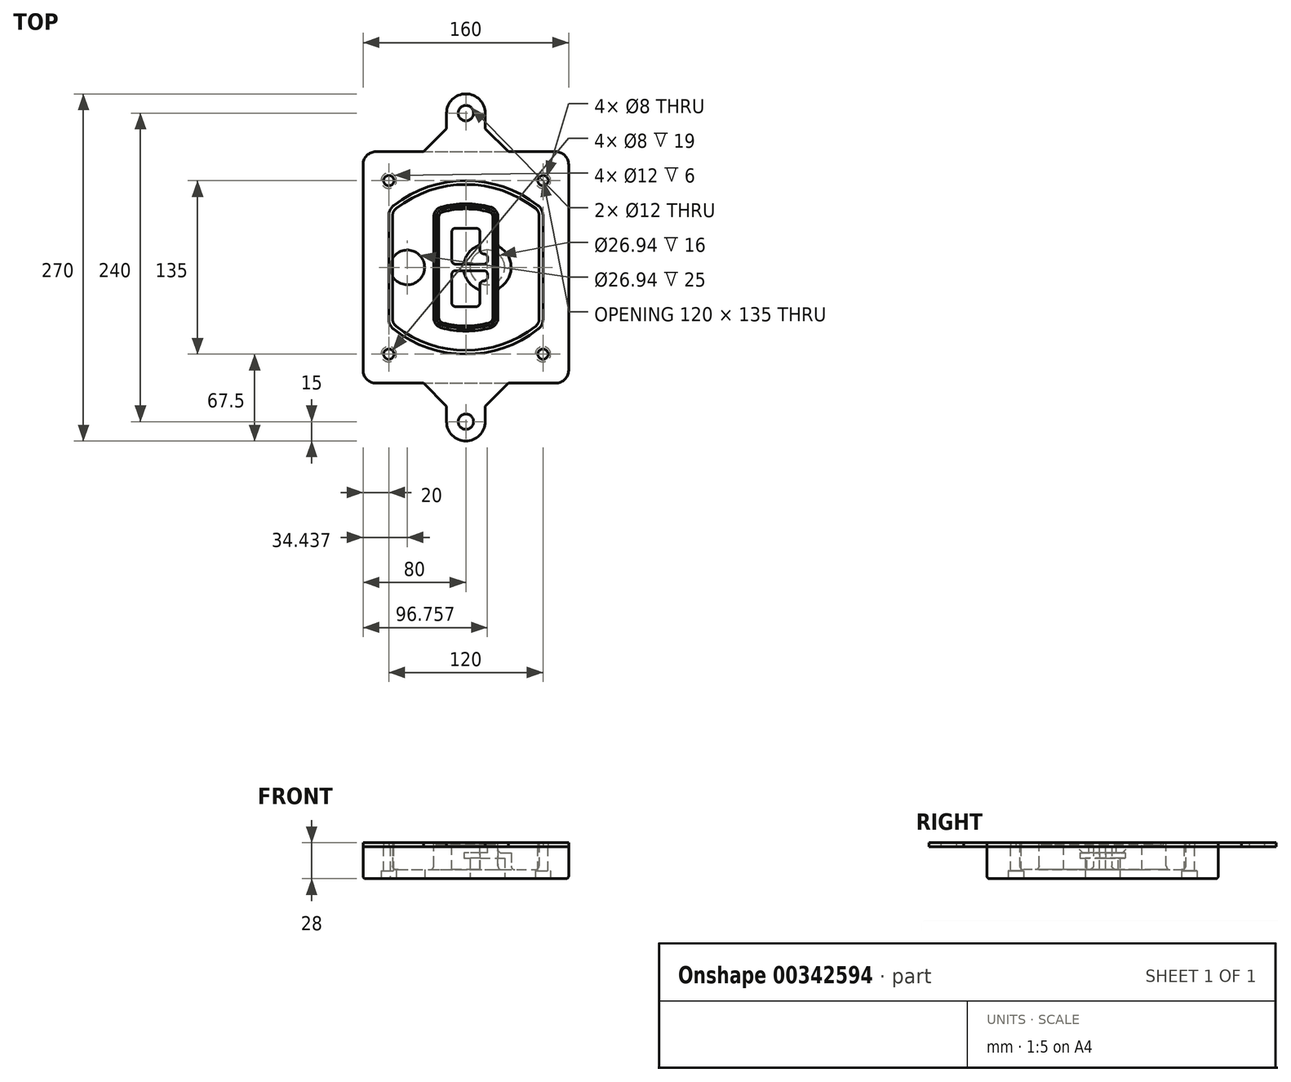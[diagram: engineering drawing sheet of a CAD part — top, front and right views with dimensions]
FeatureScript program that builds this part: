
annotation { "Feature Type Name" : "Feature", "Feature Type Description" : "" }
export const myFeature = defineFeature(function(context is Context, id is Id, definition is map)
    precondition{}
    {
        {
            var Q0;
            Q0=qCreatedBy(makeId("Top.planeOp"),FACE);
            var sketch = newSketch(context, id + "F0", { "sketchPlane" : qUnion([Q0])});
            skPoint(sketch, "E0.rect.middle", {"position": v(0, 0) * mm});
            skLineSegment(sketch, "E1.bottom", {"start": v(-70, -90) * mm, "end": v(70, -90) * mm});
            skLineSegment(sketch, "E1.top", {"start": v(-70, 90) * mm, "end": v(70, 90) * mm});
            skLineSegment(sketch, "E1.left", {"start": v(-80, -80) * mm, "end": v(-80, 80) * mm});
            skLineSegment(sketch, "E1.right", {"start": v(80, -80) * mm, "end": v(80, 80) * mm});
            skLineSegment(sketch, "E2", {"start": v(-80, 90) * mm, "end": v(80, -90) * mm, "construction": true});
            skLineSegment(sketch, "E3", {"start": v(80, 90) * mm, "end": v(-80, -90) * mm, "construction": true});
            skCircle(sketch, "E4", {"center": v(-60, 67.5) * mm, "radius": 4 * mm});
            skCircle(sketch, "E5", {"center": v(60, 67.5) * mm, "radius": 4 * mm});
            skCircle(sketch, "E6", {"center": v(60, -67.5) * mm, "radius": 4 * mm});
            skCircle(sketch, "E7", {"center": v(-60, -67.5) * mm, "radius": 4 * mm});
            skLineSegment(sketch, "E8", {"start": v(-60, 67.5) * mm, "end": v(60, 67.5) * mm, "construction": true});
            skLineSegment(sketch, "E9", {"start": v(60, 67.5) * mm, "end": v(60, -67.5) * mm, "construction": true});
            skLineSegment(sketch, "E10", {"start": v(60, -67.5) * mm, "end": v(-60, -67.5) * mm, "construction": true});
            skLineSegment(sketch, "E11", {"start": v(-60, -67.5) * mm, "end": v(-60, 67.5) * mm, "construction": true});
            skLineSegment(sketch, "E12", {"start": v(-60, 40.3) * mm, "end": v(-60, -40.3) * mm});
            skLineSegment(sketch, "E13", {"start": v(60, 40.3) * mm, "end": v(60, -40.3) * mm});
            skArc(sketch, "E14", {"start": v(56.15, 48.18) * mm, "mid": v(0, 67.5) * mm, "end": v(-56.15, 48.18) * mm});
            skArc(sketch, "E15", {"start": v(-56.15, -48.18) * mm, "mid": v(0, -67.5) * mm, "end": v(56.15, -48.18) * mm});
            skLineSegment(sketch, "E16", {"start": v(-60, 0) * mm, "end": v(60, 0) * mm, "construction": true});
            skPoint(sketch, "E17.visualSharp", {"position": v(-60, -45) * mm});
            skArc(sketch, "E17.filletArc", {"start": v(-60, -40.3) * mm, "mid": v(-58.99, -44.68) * mm, "end": v(-56.15, -48.18) * mm});
            skPoint(sketch, "E18.visualSharp", {"position": v(-60, 45) * mm});
            skArc(sketch, "E18.filletArc", {"start": v(-56.15, 48.18) * mm, "mid": v(-58.99, 44.68) * mm, "end": v(-60, 40.3) * mm});
            skPoint(sketch, "E19.visualSharp", {"position": v(60, 45) * mm});
            skArc(sketch, "E19.filletArc", {"start": v(60, 40.3) * mm, "mid": v(58.99, 44.68) * mm, "end": v(56.15, 48.18) * mm});
            skPoint(sketch, "E20.visualSharp", {"position": v(60, -45) * mm});
            skArc(sketch, "E20.filletArc", {"start": v(56.15, -48.18) * mm, "mid": v(58.99, -44.68) * mm, "end": v(60, -40.3) * mm});
            skPoint(sketch, "E21.visualSharp", {"position": v(-80, 90) * mm});
            skArc(sketch, "E21.filletArc", {"start": v(-70, 90) * mm, "mid": v(-77.07, 87.07) * mm, "end": v(-80, 80) * mm});
            skPoint(sketch, "E22.visualSharp", {"position": v(80, 90) * mm});
            skArc(sketch, "E22.filletArc", {"start": v(80, 80) * mm, "mid": v(77.07, 87.07) * mm, "end": v(70, 90) * mm});
            skPoint(sketch, "E23.visualSharp", {"position": v(80, -90) * mm});
            skArc(sketch, "E23.filletArc", {"start": v(70, -90) * mm, "mid": v(77.07, -87.07) * mm, "end": v(80, -80) * mm});
            skPoint(sketch, "E24.visualSharp", {"position": v(-80, -90) * mm});
            skArc(sketch, "E24.filletArc", {"start": v(-80, -80) * mm, "mid": v(-77.07, -87.07) * mm, "end": v(-70, -90) * mm});
            skArc(sketch, "E25.0", {"start": v(57, 40.3) * mm, "mid": v(56.3, 43.36) * mm, "end": v(54.3, 45.81) * mm});
            skLineSegment(sketch, "E25.1", {"start": v(57, 40.3) * mm, "end": v(57, -40.3) * mm});
            skArc(sketch, "E25.2", {"start": v(54.3, -45.81) * mm, "mid": v(56.3, -43.36) * mm, "end": v(57, -40.3) * mm});
            skArc(sketch, "E25.3", {"start": v(-54.3, -45.81) * mm, "mid": v(0, -64.5) * mm, "end": v(54.3, -45.81) * mm});
            skArc(sketch, "E25.4", {"start": v(-57, -40.3) * mm, "mid": v(-56.3, -43.36) * mm, "end": v(-54.3, -45.81) * mm});
            skArc(sketch, "E25.5", {"start": v(54.3, 45.81) * mm, "mid": v(0, 64.5) * mm, "end": v(-54.3, 45.81) * mm});
            skLineSegment(sketch, "E25.6", {"start": v(-57, 40.3) * mm, "end": v(-57, -40.3) * mm});
            skArc(sketch, "E25.7", {"start": v(-54.3, 45.81) * mm, "mid": v(-56.3, 43.36) * mm, "end": v(-57, 40.3) * mm});
            skArc(sketch, "E26.0", {"start": v(-58.62, 51.33) * mm, "mid": v(-62.58, 46.43) * mm, "end": v(-64, 40.3) * mm});
            skArc(sketch, "E26.1", {"start": v(58.62, 51.33) * mm, "mid": v(0, 71.5) * mm, "end": v(-58.62, 51.33) * mm});
            skArc(sketch, "E26.2", {"start": v(64, 40.3) * mm, "mid": v(62.58, 46.43) * mm, "end": v(58.62, 51.33) * mm});
            skLineSegment(sketch, "E26.3", {"start": v(64, 40.3) * mm, "end": v(64, -40.3) * mm});
            skArc(sketch, "E26.4", {"start": v(58.62, -51.33) * mm, "mid": v(62.58, -46.43) * mm, "end": v(64, -40.3) * mm});
            skLineSegment(sketch, "E26.5", {"start": v(-64, 40.3) * mm, "end": v(-64, -40.3) * mm});
            skArc(sketch, "E26.6", {"start": v(-58.62, -51.33) * mm, "mid": v(0, -71.5) * mm, "end": v(58.62, -51.33) * mm});
            skArc(sketch, "E26.7", {"start": v(-64, -40.3) * mm, "mid": v(-62.58, -46.43) * mm, "end": v(-58.62, -51.33) * mm});
            skSolve(sketch);
        }
        {
            var Q0;
            Q0=makeQuery(id+"F0.imprint","IMPRINT",FACE,{"disambiguationData":[TD([[makeQuery(id+"F0.imprint","IMPRINT",EDGE,{"derivedFrom":sQuery(id+"F0.wireOp",EDGE,"E1.bottom")}),1.0]])]});
            var Q1;
            Q1=makeQuery(id+"F0.imprint","IMPRINT",FACE,{"disambiguationData":[TD([[makeQuery(id+"F0.imprint","IMPRINT",EDGE,{"derivedFrom":sQuery(id+"F0.wireOp",EDGE,"E12")}),1.0]])]});
            var Q2;
            Q2=makeQuery(id+"F0.imprint","IMPRINT",FACE,{"disambiguationData":[TD([[makeQuery(id+"F0.imprint","IMPRINT",EDGE,{"derivedFrom":sQuery(id+"F0.wireOp",EDGE,"E25.0")}),1.0]])]});
            var Q3;
            Q3=makeQuery(id+"F0.imprint","IMPRINT",FACE,{"disambiguationData":[TD([[makeQuery(id+"F0.imprint","IMPRINT",EDGE,{"derivedFrom":sQuery(id+"F0.wireOp",EDGE,"E12")}),-1.0]])]});
            extrude(context, id + "F1", {"entities" : qUnion([Q0, Q1, Q2, Q3]), "oppositeDirection" : true, "depth" : 25 * mm});
        }
        {
            var Q0;
            Q0=makeQuery(id+"F0.imprint","IMPRINT",FACE,{"disambiguationData":[TD([[makeQuery(id+"F0.imprint","IMPRINT",EDGE,{"derivedFrom":sQuery(id+"F0.wireOp",EDGE,"E12")}),1.0]])]});
            extrude(context, id + "F2", {"entities" : qUnion([Q0]), "operationType" : NewBodyOperationType.ADD, "depth" : 3 * mm});
        }
        {
            var Q0;
            Q0=makeQuery(id+"F0.imprint","IMPRINT",FACE,{"disambiguationData":[TD([[makeQuery(id+"F0.imprint","IMPRINT",EDGE,{"derivedFrom":sQuery(id+"F0.wireOp",EDGE,"E25.0")}),1.0]])]});
            extrude(context, id + "F3", {"entities" : qUnion([Q0]), "operationType" : NewBodyOperationType.REMOVE, "oppositeDirection" : true, "depth" : 18 * mm});
        }
        {
            var Q0;
            Q0=makeQuery(id+"F2.opExtrude","CAP_FACE",FACE,{"disambiguationData":[OSD([sQuery(id+"F0.wireOp",EDGE,"E12"),sQuery(id+"F0.wireOp",EDGE,"E13"),sQuery(id+"F0.wireOp",EDGE,"E14"),sQuery(id+"F0.wireOp",EDGE,"E15"),sQuery(id+"F0.wireOp",EDGE,"E17.filletArc"),sQuery(id+"F0.wireOp",EDGE,"E18.filletArc"),sQuery(id+"F0.wireOp",EDGE,"E19.filletArc"),sQuery(id+"F0.wireOp",EDGE,"E20.filletArc"),sQuery(id+"F0.wireOp",EDGE,"E25.0"),sQuery(id+"F0.wireOp",EDGE,"E25.1"),sQuery(id+"F0.wireOp",EDGE,"E25.2"),sQuery(id+"F0.wireOp",EDGE,"E25.3"),sQuery(id+"F0.wireOp",EDGE,"E25.4"),sQuery(id+"F0.wireOp",EDGE,"E25.5"),sQuery(id+"F0.wireOp",EDGE,"E25.6"),sQuery(id+"F0.wireOp",EDGE,"E25.7")])],"isStart":false});
            var sketch = newSketch(context, id + "F4", { "sketchPlane" : qUnion([Q0])});
            skArc(sketch, "E27.0", {"start": v(-19.08, -46.97) * mm, "mid": v(0, -49.5) * mm, "end": v(19.08, -46.97) * mm});
            skArc(sketch, "E28.0", {"start": v(19.08, 46.97) * mm, "mid": v(0, 49.5) * mm, "end": v(-19.08, 46.97) * mm});
            skLineSegment(sketch, "E29", {"start": v(-25, 39.25) * mm, "end": v(-25, -39.25) * mm});
            skLineSegment(sketch, "E30", {"start": v(25, 39.25) * mm, "end": v(25, -39.25) * mm});
            skLineSegment(sketch, "E31", {"start": v(-25, 45.1) * mm, "end": v(25, 45.1) * mm, "construction": true});
            skLineSegment(sketch, "E32", {"start": v(-25, -45.1) * mm, "end": v(25, -45.1) * mm, "construction": true});
            skPoint(sketch, "E33.visualSharp", {"position": v(-25, 45.1) * mm});
            skArc(sketch, "E33.filletArc", {"start": v(-19.08, 46.97) * mm, "mid": v(-23.35, 44.11) * mm, "end": v(-25, 39.25) * mm});
            skPoint(sketch, "E34.visualSharp", {"position": v(25, 45.1) * mm});
            skArc(sketch, "E34.filletArc", {"start": v(25, 39.25) * mm, "mid": v(23.35, 44.11) * mm, "end": v(19.08, 46.97) * mm});
            skPoint(sketch, "E35.visualSharp", {"position": v(25, -45.1) * mm});
            skArc(sketch, "E35.filletArc", {"start": v(19.08, -46.97) * mm, "mid": v(23.35, -44.11) * mm, "end": v(25, -39.25) * mm});
            skPoint(sketch, "E36.visualSharp", {"position": v(-25, -45.1) * mm});
            skArc(sketch, "E36.filletArc", {"start": v(-25, -39.25) * mm, "mid": v(-23.35, -44.11) * mm, "end": v(-19.08, -46.97) * mm});
            skArc(sketch, "E37.0", {"start": v(54.3, 45.81) * mm, "mid": v(0, 64.5) * mm, "end": v(-54.3, 45.81) * mm});
            skArc(sketch, "E37.1", {"start": v(-54.3, 45.81) * mm, "mid": v(-56.3, 43.36) * mm, "end": v(-57, 40.3) * mm});
            skLineSegment(sketch, "E37.2", {"start": v(-57, 40.3) * mm, "end": v(-57, -40.3) * mm});
            skArc(sketch, "E37.3", {"start": v(-57, -40.3) * mm, "mid": v(-56.3, -43.36) * mm, "end": v(-54.3, -45.81) * mm});
            skArc(sketch, "E37.4", {"start": v(-54.3, -45.81) * mm, "mid": v(0, -64.5) * mm, "end": v(54.3, -45.81) * mm});
            skArc(sketch, "E37.5", {"start": v(54.3, -45.81) * mm, "mid": v(56.3, -43.36) * mm, "end": v(57, -40.3) * mm});
            skLineSegment(sketch, "E37.6", {"start": v(57, 40.3) * mm, "end": v(57, -40.3) * mm});
            skArc(sketch, "E37.7", {"start": v(57, 40.3) * mm, "mid": v(56.3, 43.36) * mm, "end": v(54.3, 45.81) * mm});
            skLineSegment(sketch, "E38.0", {"start": v(23, 39.25) * mm, "end": v(23, -39.25) * mm});
            skArc(sketch, "E38.1", {"start": v(18.56, -45.04) * mm, "mid": v(21.76, -42.9) * mm, "end": v(23, -39.25) * mm});
            skArc(sketch, "E38.2", {"start": v(-18.56, -45.04) * mm, "mid": v(0, -47.5) * mm, "end": v(18.56, -45.04) * mm});
            skArc(sketch, "E38.3", {"start": v(-23, -39.25) * mm, "mid": v(-21.76, -42.9) * mm, "end": v(-18.56, -45.04) * mm});
            skLineSegment(sketch, "E38.4", {"start": v(-23, 39.25) * mm, "end": v(-23, -39.25) * mm});
            skArc(sketch, "E38.5", {"start": v(23, 39.25) * mm, "mid": v(21.76, 42.9) * mm, "end": v(18.56, 45.04) * mm});
            skArc(sketch, "E38.6", {"start": v(-18.56, 45.04) * mm, "mid": v(-21.76, 42.9) * mm, "end": v(-23, 39.25) * mm});
            skArc(sketch, "E38.7", {"start": v(18.56, 45.04) * mm, "mid": v(0, 47.5) * mm, "end": v(-18.56, 45.04) * mm});
            skArc(sketch, "E39.0", {"start": v(21, 39.25) * mm, "mid": v(20.18, 41.68) * mm, "end": v(18.04, 43.1) * mm});
            skLineSegment(sketch, "E39.1", {"start": v(21, 39.25) * mm, "end": v(21, -39.25) * mm});
            skArc(sketch, "E39.2", {"start": v(18.04, -43.1) * mm, "mid": v(20.18, -41.68) * mm, "end": v(21, -39.25) * mm});
            skArc(sketch, "E39.3", {"start": v(-18.04, -43.1) * mm, "mid": v(0, -45.5) * mm, "end": v(18.04, -43.1) * mm});
            skArc(sketch, "E39.4", {"start": v(-21, -39.25) * mm, "mid": v(-20.18, -41.68) * mm, "end": v(-18.04, -43.1) * mm});
            skArc(sketch, "E39.5", {"start": v(18.04, 43.1) * mm, "mid": v(0, 45.5) * mm, "end": v(-18.04, 43.1) * mm});
            skLineSegment(sketch, "E39.6", {"start": v(-21, 39.25) * mm, "end": v(-21, -39.25) * mm});
            skArc(sketch, "E39.7", {"start": v(-18.04, 43.1) * mm, "mid": v(-20.18, 41.68) * mm, "end": v(-21, 39.25) * mm});
            skLineSegment(sketch, "E40", {"start": v(-25, 0) * mm, "end": v(25, 0) * mm, "construction": true});
            skLineSegment(sketch, "E41", {"start": v(-11, 5.5) * mm, "end": v(-11, 27.5) * mm});
            skLineSegment(sketch, "E42", {"start": v(-8, 30.5) * mm, "end": v(8, 30.5) * mm});
            skLineSegment(sketch, "E43", {"start": v(11, 27.5) * mm, "end": v(11, 13.5) * mm});
            skLineSegment(sketch, "E44", {"start": v(14, 10.5) * mm, "end": v(14, 10.5) * mm});
            skLineSegment(sketch, "E45", {"start": v(17, 7.5) * mm, "end": v(17, 5.5) * mm});
            skLineSegment(sketch, "E46", {"start": v(14, 2.5) * mm, "end": v(-8, 2.5) * mm});
            skPoint(sketch, "E47.visualSharp", {"position": v(-11, 30.5) * mm});
            skArc(sketch, "E47.filletArc", {"start": v(-8, 30.5) * mm, "mid": v(-10.12, 29.62) * mm, "end": v(-11, 27.5) * mm});
            skPoint(sketch, "E48.visualSharp", {"position": v(11, 30.5) * mm});
            skArc(sketch, "E48.filletArc", {"start": v(11, 27.5) * mm, "mid": v(10.12, 29.62) * mm, "end": v(8, 30.5) * mm});
            skPoint(sketch, "E49.visualSharp", {"position": v(11, 10.5) * mm});
            skArc(sketch, "E49.filletArc", {"start": v(11, 13.5) * mm, "mid": v(11.88, 11.38) * mm, "end": v(14, 10.5) * mm});
            skPoint(sketch, "E50.visualSharp", {"position": v(17, 10.5) * mm});
            skArc(sketch, "E50.filletArc", {"start": v(17, 7.5) * mm, "mid": v(16.12, 9.62) * mm, "end": v(14, 10.5) * mm});
            skPoint(sketch, "E51.visualSharp", {"position": v(17, 2.5) * mm});
            skArc(sketch, "E51.filletArc", {"start": v(14, 2.5) * mm, "mid": v(16.12, 3.38) * mm, "end": v(17, 5.5) * mm});
            skPoint(sketch, "E52.visualSharp", {"position": v(-11, 2.5) * mm});
            skArc(sketch, "E52.filletArc", {"start": v(-11, 5.5) * mm, "mid": v(-10.12, 3.38) * mm, "end": v(-8, 2.5) * mm});
            skLineSegment(sketch, "E53.0.MirrorCS", {"start": v(14, -2.5) * mm, "end": v(-8, -2.5) * mm});
            skArc(sketch, "E54.0.MirrorCS", {"start": v(-11, -5.5) * mm, "mid": v(-10.12, -3.38) * mm, "end": v(-8, -2.5) * mm});
            skLineSegment(sketch, "E55.0.MirrorCS", {"start": v(-11, -5.5) * mm, "end": v(-11, -27.5) * mm});
            skArc(sketch, "E56.0.MirrorCS", {"start": v(-8, -30.5) * mm, "mid": v(-10.12, -29.62) * mm, "end": v(-11, -27.5) * mm});
            skLineSegment(sketch, "E57.0.MirrorCS", {"start": v(-8, -30.5) * mm, "end": v(8, -30.5) * mm});
            skArc(sketch, "E58.0.MirrorCS", {"start": v(11, -27.5) * mm, "mid": v(10.12, -29.62) * mm, "end": v(8, -30.5) * mm});
            skLineSegment(sketch, "E59.0.MirrorCS", {"start": v(11, -27.5) * mm, "end": v(11, -13.5) * mm});
            skArc(sketch, "E60.0.MirrorCS", {"start": v(11, -13.5) * mm, "mid": v(11.88, -11.38) * mm, "end": v(14, -10.5) * mm});
            skArc(sketch, "E61.0.MirrorCS", {"start": v(17, -7.5) * mm, "mid": v(16.12, -9.62) * mm, "end": v(14, -10.5) * mm});
            skLineSegment(sketch, "E62.0.MirrorCS", {"start": v(17, -7.5) * mm, "end": v(17, -5.5) * mm});
            skArc(sketch, "E63.0.MirrorCS", {"start": v(14, -2.5) * mm, "mid": v(16.12, -3.38) * mm, "end": v(17, -5.5) * mm});
            skSolve(sketch);
        }
        {
            var Q0;
            Q0=makeQuery(id+"F4.imprint","IMPRINT",FACE,{"disambiguationData":[TD([[makeQuery(id+"F4.imprint","IMPRINT",EDGE,{"derivedFrom":sQuery(id+"F4.wireOp",EDGE,"E27.0")}),1.0]])]});
            var Q1;
            Q1=makeQuery(id+"F4.imprint","IMPRINT",FACE,{"disambiguationData":[TD([[makeQuery(id+"F4.imprint","IMPRINT",EDGE,{"derivedFrom":sQuery(id+"F4.wireOp",EDGE,"E38.0")}),-1.0]])]});
            var Q2;
            Q2=makeQuery(id+"F4.imprint","IMPRINT",FACE,{"disambiguationData":[TD([[makeQuery(id+"F4.imprint","IMPRINT",EDGE,{"derivedFrom":sQuery(id+"F4.wireOp",EDGE,"E39.0")}),1.0]])]});
            extrude(context, id + "F5", {"entities" : qUnion([Q0, Q1, Q2]), "operationType" : NewBodyOperationType.ADD, "endBound" : BoundingType.UP_TO_NEXT, "oppositeDirection" : true, "depth" : 25 * mm});
        }
        {
            var Q0;
            Q0=makeQuery(id+"F4.imprint","IMPRINT",FACE,{"disambiguationData":[TD([[makeQuery(id+"F4.imprint","IMPRINT",EDGE,{"derivedFrom":sQuery(id+"F4.wireOp",EDGE,"E38.0")}),-1.0]])]});
            extrude(context, id + "F6", {"entities" : qUnion([Q0]), "operationType" : NewBodyOperationType.REMOVE, "oppositeDirection" : true, "depth" : 2 * mm});
        }
        {
            var Q0;
            Q0=makeQuery(id+"F1.opExtrude","CAP_FACE",FACE,{"disambiguationData":[OSD([sQuery(id+"F0.wireOp",EDGE,"E1.bottom"),sQuery(id+"F0.wireOp",EDGE,"E1.top"),sQuery(id+"F0.wireOp",EDGE,"E1.left"),sQuery(id+"F0.wireOp",EDGE,"E1.right"),sQuery(id+"F0.wireOp",EDGE,"E4"),sQuery(id+"F0.wireOp",EDGE,"E5"),sQuery(id+"F0.wireOp",EDGE,"E6"),sQuery(id+"F0.wireOp",EDGE,"E7"),sQuery(id+"F0.wireOp",EDGE,"E21.filletArc"),sQuery(id+"F0.wireOp",EDGE,"E22.filletArc"),sQuery(id+"F0.wireOp",EDGE,"E23.filletArc"),sQuery(id+"F0.wireOp",EDGE,"E24.filletArc")])],"isStart":false});
            var sketch = newSketch(context, id + "F7", { "sketchPlane" : qUnion([Q0])});
            skCircle(sketch, "E64", {"center": v(16.76, 0) * mm, "radius": 13.47 * mm});
            skCircle(sketch, "E65", {"center": v(-45.56, 0) * mm, "radius": 13.47 * mm});
            skLineSegment(sketch, "E66", {"start": v(80, 0) * mm, "end": v(-80, 0) * mm});
            skCircle(sketch, "E67", {"center": v(16.76, 0) * mm, "radius": 18.47 * mm});
            skCircle(sketch, "E68", {"center": v(60, -67.5) * mm, "radius": 6 * mm});
            skCircle(sketch, "E69", {"center": v(-60, -67.5) * mm, "radius": 6 * mm});
            skCircle(sketch, "E70", {"center": v(-60, 67.5) * mm, "radius": 6 * mm});
            skCircle(sketch, "E71", {"center": v(60, 67.5) * mm, "radius": 6 * mm});
            skSolve(sketch);
        }
        {
            var Q0;
            {var subQ1=sQuery(id+"F7.wireOp",EDGE,"E66");var subQ4=sQuery(id+"F7.wireOp",EDGE,"E64");var subQ6=makeQuery(id+"F7.imprint","INTERSECT",VERTEX,{"disambiguationData":[OD(0.0)],"derivedFrom":[subQ4,subQ1]});Q0=makeQuery(id+"F7.imprint","IMPRINT",FACE,{"disambiguationData":[TD([[makeQuery(id+"F7.imprint","IMPRINT",EDGE,{"disambiguationData":[TD([[subQ6,-1.0]])],"derivedFrom":subQ4}),-1.0]])]});}
            var Q1;
            {var subQ0=sQuery(id+"F7.wireOp",EDGE,"E66");var subQ1=sQuery(id+"F7.wireOp",EDGE,"E64");var subQ3=makeQuery(id+"F7.imprint","INTERSECT",VERTEX,{"disambiguationData":[OD(0.0)],"derivedFrom":[subQ1,subQ0]});Q1=makeQuery(id+"F7.imprint","IMPRINT",FACE,{"disambiguationData":[TD([[makeQuery(id+"F7.imprint","IMPRINT",EDGE,{"disambiguationData":[TD([[subQ3,-1.0]])],"derivedFrom":subQ1}),1.0]])]});}
            var Q2;
            {var subQ0=sQuery(id+"F7.wireOp",EDGE,"E66");var subQ1=sQuery(id+"F7.wireOp",EDGE,"E64");var subQ3=makeQuery(id+"F7.imprint","INTERSECT",VERTEX,{"disambiguationData":[OD(0.0)],"derivedFrom":[subQ1,subQ0]});Q2=makeQuery(id+"F7.imprint","IMPRINT",FACE,{"disambiguationData":[TD([[makeQuery(id+"F7.imprint","IMPRINT",EDGE,{"disambiguationData":[TD([[subQ3,1.0]])],"derivedFrom":subQ1}),1.0]])]});}
            var Q3;
            {var subQ1=sQuery(id+"F7.wireOp",EDGE,"E66");var subQ4=sQuery(id+"F7.wireOp",EDGE,"E64");var subQ6=makeQuery(id+"F7.imprint","INTERSECT",VERTEX,{"disambiguationData":[OD(0.0)],"derivedFrom":[subQ4,subQ1]});Q3=makeQuery(id+"F7.imprint","IMPRINT",FACE,{"disambiguationData":[TD([[makeQuery(id+"F7.imprint","IMPRINT",EDGE,{"disambiguationData":[TD([[subQ6,1.0]])],"derivedFrom":subQ4}),-1.0]])]});}
            extrude(context, id + "F8", {"entities" : qUnion([Q0, Q1, Q2, Q3]), "operationType" : NewBodyOperationType.ADD, "oppositeDirection" : true, "depth" : 20 * mm});
        }
        {
            var Q0;
            {var subQ0=sQuery(id+"F7.wireOp",EDGE,"E66");var subQ1=sQuery(id+"F7.wireOp",EDGE,"E64");var subQ3=makeQuery(id+"F7.imprint","INTERSECT",VERTEX,{"disambiguationData":[OD(0.0)],"derivedFrom":[subQ1,subQ0]});Q0=makeQuery(id+"F7.imprint","IMPRINT",FACE,{"disambiguationData":[TD([[makeQuery(id+"F7.imprint","IMPRINT",EDGE,{"disambiguationData":[TD([[subQ3,-1.0]])],"derivedFrom":subQ1}),1.0]])]});}
            var Q1;
            {var subQ0=sQuery(id+"F7.wireOp",EDGE,"E66");var subQ1=sQuery(id+"F7.wireOp",EDGE,"E64");var subQ3=makeQuery(id+"F7.imprint","INTERSECT",VERTEX,{"disambiguationData":[OD(0.0)],"derivedFrom":[subQ1,subQ0]});Q1=makeQuery(id+"F7.imprint","IMPRINT",FACE,{"disambiguationData":[TD([[makeQuery(id+"F7.imprint","IMPRINT",EDGE,{"disambiguationData":[TD([[subQ3,1.0]])],"derivedFrom":subQ1}),1.0]])]});}
            extrude(context, id + "F9", {"entities" : qUnion([Q0, Q1]), "operationType" : NewBodyOperationType.REMOVE, "oppositeDirection" : true, "depth" : 16 * mm});
        }
        {
            var Q0;
            {var subQ0=sQuery(id+"F7.wireOp",EDGE,"E66");var subQ1=sQuery(id+"F7.wireOp",EDGE,"E65");var subQ3=makeQuery(id+"F7.imprint","INTERSECT",VERTEX,{"disambiguationData":[OD(0.0)],"derivedFrom":[subQ1,subQ0]});Q0=makeQuery(id+"F7.imprint","IMPRINT",FACE,{"disambiguationData":[TD([[makeQuery(id+"F7.imprint","IMPRINT",EDGE,{"disambiguationData":[TD([[subQ3,-1.0]])],"derivedFrom":subQ1}),1.0]])]});}
            var Q1;
            {var subQ0=sQuery(id+"F7.wireOp",EDGE,"E66");var subQ1=sQuery(id+"F7.wireOp",EDGE,"E65");var subQ3=makeQuery(id+"F7.imprint","INTERSECT",VERTEX,{"disambiguationData":[OD(0.0)],"derivedFrom":[subQ1,subQ0]});Q1=makeQuery(id+"F7.imprint","IMPRINT",FACE,{"disambiguationData":[TD([[makeQuery(id+"F7.imprint","IMPRINT",EDGE,{"disambiguationData":[TD([[subQ3,1.0]])],"derivedFrom":subQ1}),1.0]])]});}
            extrude(context, id + "F10", {"entities" : qUnion([Q0, Q1]), "operationType" : NewBodyOperationType.REMOVE, "oppositeDirection" : true, "depth" : 25 * mm});
        }
        {
            var Q0;
            Q0=makeQuery(id+"F7.imprint","IMPRINT",FACE,{"disambiguationData":[TD([[makeQuery(id+"F7.imprint","IMPRINT",EDGE,{"derivedFrom":sQuery(id+"F7.wireOp",EDGE,"E68")}),1.0]])]});
            var Q1;
            Q1=makeQuery(id+"F7.imprint","IMPRINT",FACE,{"disambiguationData":[TD([[makeQuery(id+"F7.imprint","IMPRINT",EDGE,{"derivedFrom":makeQuery(id+"F1.opExtrude","CAP_EDGE",EDGE,{"disambiguationData":[OSD([sQuery(id+"F0.wireOp",EDGE,"E5")])],"isStart":false})}),-1.0]])]});
            var Q2;
            Q2=makeQuery(id+"F7.imprint","IMPRINT",FACE,{"disambiguationData":[TD([[makeQuery(id+"F7.imprint","IMPRINT",EDGE,{"derivedFrom":sQuery(id+"F7.wireOp",EDGE,"E69")}),1.0]])]});
            var Q3;
            Q3=makeQuery(id+"F7.imprint","IMPRINT",FACE,{"disambiguationData":[TD([[makeQuery(id+"F7.imprint","IMPRINT",EDGE,{"derivedFrom":makeQuery(id+"F1.opExtrude","CAP_EDGE",EDGE,{"disambiguationData":[OSD([sQuery(id+"F0.wireOp",EDGE,"E4")])],"isStart":false})}),-1.0]])]});
            var Q4;
            Q4=makeQuery(id+"F7.imprint","IMPRINT",FACE,{"disambiguationData":[TD([[makeQuery(id+"F7.imprint","IMPRINT",EDGE,{"derivedFrom":sQuery(id+"F7.wireOp",EDGE,"E70")}),1.0]])]});
            var Q5;
            Q5=makeQuery(id+"F7.imprint","IMPRINT",FACE,{"disambiguationData":[TD([[makeQuery(id+"F7.imprint","IMPRINT",EDGE,{"derivedFrom":makeQuery(id+"F1.opExtrude","CAP_EDGE",EDGE,{"disambiguationData":[OSD([sQuery(id+"F0.wireOp",EDGE,"E7")])],"isStart":false})}),-1.0]])]});
            var Q6;
            Q6=makeQuery(id+"F7.imprint","IMPRINT",FACE,{"disambiguationData":[TD([[makeQuery(id+"F7.imprint","IMPRINT",EDGE,{"derivedFrom":sQuery(id+"F7.wireOp",EDGE,"E71")}),1.0]])]});
            var Q7;
            Q7=makeQuery(id+"F7.imprint","IMPRINT",FACE,{"disambiguationData":[TD([[makeQuery(id+"F7.imprint","IMPRINT",EDGE,{"derivedFrom":makeQuery(id+"F1.opExtrude","CAP_EDGE",EDGE,{"disambiguationData":[OSD([sQuery(id+"F0.wireOp",EDGE,"E6")])],"isStart":false})}),-1.0]])]});
            extrude(context, id + "F11", {"entities" : qUnion([Q0, Q1, Q2, Q3, Q4, Q5, Q6, Q7]), "operationType" : NewBodyOperationType.REMOVE, "oppositeDirection" : true, "depth" : 6 * mm});
        }
        {
            var Q0;
            Q0=makeQuery(id+"F9.boolean.opBoolean","COPY",FACE,{"derivedFrom":makeQuery(id+"F9.opExtrude","CAP_FACE",FACE,{"disambiguationData":[OSD([sQuery(id+"F7.wireOp",EDGE,"E64")])],"isStart":false})});
            var sketch = newSketch(context, id + "F12", { "sketchPlane" : qUnion([Q0])});
            skArc(sketch, "E72.0", {"start": v(11, 17.55) * mm, "mid": v(2.57, 11.82) * mm, "end": v(-1.54, 2.5) * mm});
            skArc(sketch, "E72.1", {"start": v(-1.54, -2.5) * mm, "mid": v(2.57, -11.82) * mm, "end": v(11, -17.55) * mm});
            skLineSegment(sketch, "E73", {"start": v(-1.54, -2.5) * mm, "end": v(14, -2.5) * mm});
            skLineSegment(sketch, "E74.0", {"start": v(14, 2.5) * mm, "end": v(-1.54, 2.5) * mm});
            skArc(sketch, "E74.1", {"start": v(14, 2.5) * mm, "mid": v(16.12, 3.38) * mm, "end": v(17, 5.5) * mm});
            skLineSegment(sketch, "E74.2", {"start": v(17, 7.5) * mm, "end": v(17, 5.5) * mm});
            skArc(sketch, "E74.3", {"start": v(17, 7.5) * mm, "mid": v(16.12, 9.62) * mm, "end": v(14, 10.5) * mm});
            skArc(sketch, "E74.4", {"start": v(11, 13.5) * mm, "mid": v(11.88, 11.38) * mm, "end": v(14, 10.5) * mm});
            skLineSegment(sketch, "E74.5", {"start": v(11, 17.55) * mm, "end": v(11, 13.5) * mm});
            skLineSegment(sketch, "E74.7", {"start": v(14, -2.5) * mm, "end": v(-1.54, -2.5) * mm});
            skArc(sketch, "E74.8", {"start": v(14, -2.5) * mm, "mid": v(16.12, -3.38) * mm, "end": v(17, -5.5) * mm});
            skLineSegment(sketch, "E74.9", {"start": v(17, -7.5) * mm, "end": v(17, -5.5) * mm});
            skArc(sketch, "E74.10", {"start": v(17, -7.5) * mm, "mid": v(16.12, -9.62) * mm, "end": v(14, -10.5) * mm});
            skArc(sketch, "E74.11", {"start": v(11, -13.5) * mm, "mid": v(11.88, -11.38) * mm, "end": v(14, -10.5) * mm});
            skLineSegment(sketch, "E74.12", {"start": v(11, -17.55) * mm, "end": v(11, -13.5) * mm});
            skPoint(sketch, "E75.orphan", {"position": v(11, -27.5) * mm});
            skPoint(sketch, "E76.orphan", {"position": v(-8, -2.5) * mm});
            skPoint(sketch, "E77.orphan", {"position": v(-8, 2.5) * mm});
            skPoint(sketch, "E78.orphan", {"position": v(11, 27.5) * mm});
            skSolve(sketch);
        }
        {
            var Q0;
            {var subQ7=sQuery(id+"F12.wireOp",EDGE,"E72.0");var subQ14=sQuery(id+"F12.wireOp",EDGE,"E72.1");var subQ16=sQuery(id+"F12.wireOp",EDGE,"E74.1");var subQ18=sQuery(id+"F12.wireOp",EDGE,"E74.8");Q0=qUnion([makeQuery(id+"F12.imprint","IMPRINT",FACE,{"disambiguationData":[TD([[makeQuery(id+"F12.imprint","IMPRINT",EDGE,{"derivedFrom":subQ7}),1.0]])]}),makeQuery(id+"F12.imprint","IMPRINT",FACE,{"disambiguationData":[TD([[makeQuery(id+"F12.imprint","IMPRINT",EDGE,{"derivedFrom":subQ14}),1.0]])]}),makeQuery(id+"F12.imprint","IMPRINT",FACE,{"disambiguationData":[TD([[makeQuery(id+"F12.imprint","IMPRINT",EDGE,{"derivedFrom":subQ16}),1.0]])]}),makeQuery(id+"F12.imprint","IMPRINT",FACE,{"disambiguationData":[TD([[makeQuery(id+"F12.imprint","IMPRINT",EDGE,{"derivedFrom":subQ18}),-1.0]])]})]);}
            var Q1;
            Q1=makeQuery(id+"F5.boolean.opBoolean","SPLIT",FACE,{"disambiguationData":[TD([makeQuery(id+"F5.opExtrude","SWEPT_FACE",FACE,{"disambiguationData":[OSD([sQuery(id+"F4.wireOp",EDGE,"E41")])]})])],"derivedFrom":makeQuery(id+"F3.boolean.opBoolean","COPY",FACE,{"derivedFrom":makeQuery(id+"F3.opExtrude","CAP_FACE",FACE,{"disambiguationData":[OSD([sQuery(id+"F0.wireOp",EDGE,"E25.0"),sQuery(id+"F0.wireOp",EDGE,"E25.1"),sQuery(id+"F0.wireOp",EDGE,"E25.2"),sQuery(id+"F0.wireOp",EDGE,"E25.3"),sQuery(id+"F0.wireOp",EDGE,"E25.4"),sQuery(id+"F0.wireOp",EDGE,"E25.5"),sQuery(id+"F0.wireOp",EDGE,"E25.6"),sQuery(id+"F0.wireOp",EDGE,"E25.7")])],"isStart":false})})});
            extrude(context, id + "F13", {"entities" : qUnion([Q0]), "operationType" : NewBodyOperationType.REMOVE, "endBound" : BoundingType.UP_TO_SURFACE, "endBoundEntityFace" : qUnion([Q1]), "depth" : 25 * mm});
        }
        {
            var Q0;
            Q0=makeQuery(id+"F3.boolean.opBoolean","COPY",EDGE,{"derivedFrom":makeQuery(id+"F3.opExtrude","CAP_EDGE",EDGE,{"disambiguationData":[OSD([sQuery(id+"F0.wireOp",EDGE,"E25.6")])],"isStart":false})});
            var Q1;
            Q1=makeQuery(id+"F8.boolean.opBoolean","INTERSECT",EDGE,{"derivedFrom":[makeQuery(id+"F5.opExtrude","SWEPT_FACE",FACE,{"disambiguationData":[OSD([sQuery(id+"F4.wireOp",EDGE,"E30")])]}),makeQuery(id+"F8.opExtrude","CAP_FACE",FACE,{"disambiguationData":[OSD([sQuery(id+"F7.wireOp",EDGE,"E67")])],"isStart":false})]});
            var Q2;
            Q2=makeQuery(id+"F8.boolean.opBoolean","INTERSECT",EDGE,{"disambiguationData":[OD(1.0)],"derivedFrom":[makeQuery(id+"F5.opExtrude","SWEPT_FACE",FACE,{"disambiguationData":[OSD([sQuery(id+"F4.wireOp",EDGE,"E30")])]}),makeQuery(id+"F8.opExtrude","SWEPT_FACE",FACE,{"disambiguationData":[OSD([sQuery(id+"F7.wireOp",EDGE,"E67")])]})]});
            var Q3;
            {var subQ0=sQuery(id+"F4.wireOp",EDGE,"E30");Q3=makeQuery(id+"F8.boolean.opBoolean","SPLIT",EDGE,{"disambiguationData":[TD([makeQuery(id+"F5.opExtrude","SWEPT_FACE",FACE,{"disambiguationData":[OSD([sQuery(id+"F4.wireOp",EDGE,"E35.filletArc")])]})])],"derivedFrom":makeQuery(id+"F5.opExtrude","CAP_EDGE",EDGE,{"disambiguationData":[OSD([subQ0])],"isStart":false})});}
            var Q4;
            {var subQ0=sQuery(id+"F0.wireOp",EDGE,"E25.7");var subQ1=sQuery(id+"F0.wireOp",EDGE,"E25.1");var subQ2=sQuery(id+"F0.wireOp",EDGE,"E25.6");var subQ3=sQuery(id+"F0.wireOp",EDGE,"E25.5");var subQ4=sQuery(id+"F0.wireOp",EDGE,"E25.4");var subQ5=sQuery(id+"F0.wireOp",EDGE,"E25.0");var subQ6=sQuery(id+"F0.wireOp",EDGE,"E25.2");var subQ7=sQuery(id+"F0.wireOp",EDGE,"E25.3");Q4=makeQuery(id+"F8.boolean.opBoolean","INTERSECT",EDGE,{"derivedFrom":[makeQuery(id+"F5.boolean.opBoolean","SPLIT",FACE,{"disambiguationData":[TD([makeQuery(id+"F2.opExtrude","SWEPT_FACE",FACE,{"disambiguationData":[OSD([subQ5])]})])],"derivedFrom":makeQuery(id+"F3.boolean.opBoolean","COPY",FACE,{"derivedFrom":makeQuery(id+"F3.opExtrude","CAP_FACE",FACE,{"disambiguationData":[OSD([subQ5,subQ1,subQ6,subQ7,subQ4,subQ3,subQ2,subQ0])],"isStart":false})})}),makeQuery(id+"F8.opExtrude","SWEPT_FACE",FACE,{"disambiguationData":[OSD([sQuery(id+"F7.wireOp",EDGE,"E67")])]})]});}
            var Q5;
            Q5=makeQuery(id+"F8.boolean.opBoolean","INTERSECT",EDGE,{"disambiguationData":[OD(0.0)],"derivedFrom":[makeQuery(id+"F5.opExtrude","SWEPT_FACE",FACE,{"disambiguationData":[OSD([sQuery(id+"F4.wireOp",EDGE,"E30")])]}),makeQuery(id+"F8.opExtrude","SWEPT_FACE",FACE,{"disambiguationData":[OSD([sQuery(id+"F7.wireOp",EDGE,"E67")])]})]});
            fillet(context, id + "F14", {"entities" : qUnion([Q0, Q1, Q2, Q3, Q4, Q5]), "radius" : 3 * mm, "tangentPropagation" : true, "allowEdgeOverflow" : false});
        }
        {
            var Q0;
            Q0=makeQuery(id+"F1.opExtrude","CAP_EDGE",EDGE,{"disambiguationData":[OSD([sQuery(id+"F0.wireOp",EDGE,"E1.bottom")])],"isStart":false});
            fillet(context, id + "F15", {"entities" : qUnion([Q0]), "radius" : 2 * mm, "tangentPropagation" : true, "allowEdgeOverflow" : false});
        }
        {
            var Q0;
            {var subQ0=sQuery(id+"F0.wireOp",EDGE,"E21.filletArc");var subQ1=sQuery(id+"F0.wireOp",EDGE,"E7");var subQ2=sQuery(id+"F0.wireOp",EDGE,"E6");var subQ3=sQuery(id+"F0.wireOp",EDGE,"E5");var subQ4=sQuery(id+"F0.wireOp",EDGE,"E4");var subQ5=sQuery(id+"F0.wireOp",EDGE,"E22.filletArc");var subQ6=sQuery(id+"F0.wireOp",EDGE,"E1.bottom");var subQ7=sQuery(id+"F0.wireOp",EDGE,"E1.right");var subQ8=sQuery(id+"F0.wireOp",EDGE,"E1.top");var subQ9=sQuery(id+"F0.wireOp",EDGE,"E1.left");var subQ10=sQuery(id+"F0.wireOp",EDGE,"E23.filletArc");var subQ11=sQuery(id+"F0.wireOp",EDGE,"E24.filletArc");Q0=makeQuery(id+"F2.boolean.opBoolean","SPLIT",FACE,{"disambiguationData":[TD([makeQuery(id+"F1.opExtrude","SWEPT_FACE",FACE,{"disambiguationData":[OSD([subQ6])]})])],"derivedFrom":makeQuery(id+"F1.opExtrude","CAP_FACE",FACE,{"disambiguationData":[OSD([subQ6,subQ8,subQ9,subQ7,subQ4,subQ3,subQ2,subQ1,subQ0,subQ5,subQ10,subQ11])],"isStart":true})});}
            var sketch = newSketch(context, id + "F16", { "sketchPlane" : qUnion([Q0])});
            skArc(sketch, "E79.0", {"start": v(-56.15, -48.18) * mm, "mid": v(0, -67.5) * mm, "end": v(56.15, -48.18) * mm});
            skLineSegment(sketch, "E79.1", {"start": v(-60, 40.3) * mm, "end": v(-60, -40.3) * mm});
            skArc(sketch, "E79.2", {"start": v(-60, -40.3) * mm, "mid": v(-58.99, -44.68) * mm, "end": v(-56.15, -48.18) * mm});
            skArc(sketch, "E79.3", {"start": v(56.15, 48.18) * mm, "mid": v(0, 67.5) * mm, "end": v(-56.15, 48.18) * mm});
            skLineSegment(sketch, "E79.4", {"start": v(60, 40.3) * mm, "end": v(60, -40.3) * mm});
            skArc(sketch, "E79.5", {"start": v(60, 40.3) * mm, "mid": v(58.99, 44.68) * mm, "end": v(56.15, 48.18) * mm});
            skArc(sketch, "E79.6", {"start": v(-56.15, 48.18) * mm, "mid": v(-58.99, 44.68) * mm, "end": v(-60, 40.3) * mm});
            skArc(sketch, "E79.7", {"start": v(56.15, -48.18) * mm, "mid": v(58.99, -44.68) * mm, "end": v(60, -40.3) * mm});
            skLineSegment(sketch, "E79.8", {"start": v(80, -80) * mm, "end": v(80, 80) * mm});
            skArc(sketch, "E79.9", {"start": v(80, 80) * mm, "mid": v(77.07, 87.07) * mm, "end": v(70, 90) * mm});
            skLineSegment(sketch, "E79.10", {"start": v(-70, 90) * mm, "end": v(70, 90) * mm});
            skArc(sketch, "E79.11", {"start": v(-70, 90) * mm, "mid": v(-77.07, 87.07) * mm, "end": v(-80, 80) * mm});
            skLineSegment(sketch, "E79.12", {"start": v(-80, -80) * mm, "end": v(-80, 80) * mm});
            skArc(sketch, "E79.13", {"start": v(-80, -80) * mm, "mid": v(-77.07, -87.07) * mm, "end": v(-70, -90) * mm});
            skLineSegment(sketch, "E79.14", {"start": v(-70, -90) * mm, "end": v(70, -90) * mm});
            skArc(sketch, "E79.15", {"start": v(70, -90) * mm, "mid": v(77.07, -87.07) * mm, "end": v(80, -80) * mm});
            skCircle(sketch, "E79.16", {"center": v(60, -67.5) * mm, "radius": 4 * mm});
            skCircle(sketch, "E79.17", {"center": v(60, 67.5) * mm, "radius": 4 * mm});
            skCircle(sketch, "E79.18", {"center": v(-60, 67.5) * mm, "radius": 4 * mm});
            skCircle(sketch, "E79.19", {"center": v(-60, -67.5) * mm, "radius": 4 * mm});
            skLineSegment(sketch, "E80", {"start": v(-33, 90) * mm, "end": v(-15, 108) * mm});
            skLineSegment(sketch, "E81", {"start": v(33, 90) * mm, "end": v(15, 108) * mm});
            skLineSegment(sketch, "E82", {"start": v(15, 108) * mm, "end": v(15, 120) * mm});
            skLineSegment(sketch, "E83", {"start": v(-15, 108) * mm, "end": v(-15, 120) * mm});
            skArc(sketch, "E84", {"start": v(15, 120) * mm, "mid": v(0, 135) * mm, "end": v(-15, 120) * mm});
            skCircle(sketch, "E85", {"center": v(0, 120) * mm, "radius": 6 * mm});
            skLineSegment(sketch, "E86", {"start": v(0, 90) * mm, "end": v(0, 120) * mm, "construction": true});
            skLineSegment(sketch, "E87", {"start": v(-80, 0) * mm, "end": v(80, 0) * mm, "construction": true});
            skLineSegment(sketch, "E88.MirrorCS", {"start": v(-33, -90) * mm, "end": v(-15, -108) * mm});
            skLineSegment(sketch, "E89.MirrorCS", {"start": v(-15, -108) * mm, "end": v(-15, -120) * mm});
            skArc(sketch, "E90.MirrorCS", {"start": v(15, -120) * mm, "mid": v(0, -135) * mm, "end": v(-15, -120) * mm});
            skLineSegment(sketch, "E91.MirrorCS", {"start": v(15, -108) * mm, "end": v(15, -120) * mm});
            skLineSegment(sketch, "E92.MirrorCS", {"start": v(33, -90) * mm, "end": v(15, -108) * mm});
            skLineSegment(sketch, "E93.MirrorCS", {"start": v(0, -90) * mm, "end": v(0, -120) * mm, "construction": true});
            skCircle(sketch, "E94.MirrorC", {"center": v(0, -120) * mm, "radius": 6 * mm});
            skSolve(sketch);
        }
        {
            var Q0;
            Q0 = qSketchRegion(id + "F16", true);
            var Q1;
            Q1=makeQuery(id+"F2.opExtrude","CAP_FACE",FACE,{"disambiguationData":[OSD([sQuery(id+"F0.wireOp",EDGE,"E12"),sQuery(id+"F0.wireOp",EDGE,"E13"),sQuery(id+"F0.wireOp",EDGE,"E14"),sQuery(id+"F0.wireOp",EDGE,"E15"),sQuery(id+"F0.wireOp",EDGE,"E17.filletArc"),sQuery(id+"F0.wireOp",EDGE,"E18.filletArc"),sQuery(id+"F0.wireOp",EDGE,"E19.filletArc"),sQuery(id+"F0.wireOp",EDGE,"E20.filletArc"),sQuery(id+"F0.wireOp",EDGE,"E25.0"),sQuery(id+"F0.wireOp",EDGE,"E25.1"),sQuery(id+"F0.wireOp",EDGE,"E25.2"),sQuery(id+"F0.wireOp",EDGE,"E25.3"),sQuery(id+"F0.wireOp",EDGE,"E25.4"),sQuery(id+"F0.wireOp",EDGE,"E25.5"),sQuery(id+"F0.wireOp",EDGE,"E25.6"),sQuery(id+"F0.wireOp",EDGE,"E25.7")])],"isStart":false});
            extrude(context, id + "F17", {"entities" : qUnion([Q0]), "endBound" : BoundingType.UP_TO_SURFACE, "endBoundEntityFace" : qUnion([Q1]), "depth" : 25 * mm});
        }
    });
